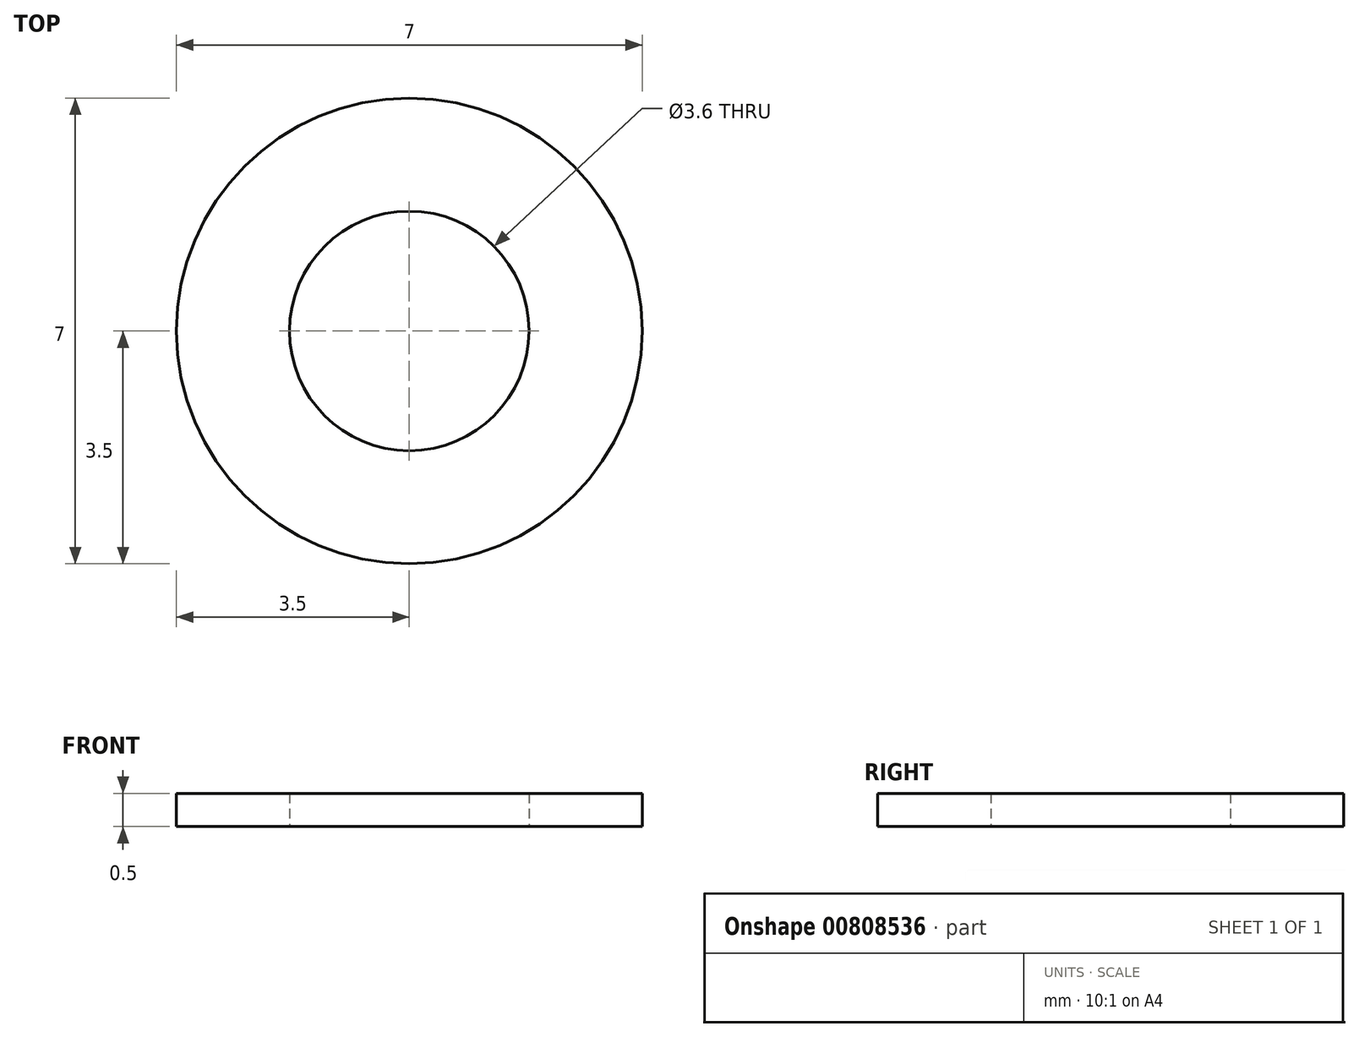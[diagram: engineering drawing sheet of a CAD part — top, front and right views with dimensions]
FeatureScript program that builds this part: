
annotation { "Feature Type Name" : "Feature", "Feature Type Description" : "" }
export const myFeature = defineFeature(function(context is Context, id is Id, definition is map)
    precondition{}
    {
        {
            var Q0;
            Q0=qCreatedBy(makeId("Top.planeOp"),FACE);
            var sketch = newSketch(context, id + "F0", { "sketchPlane" : qUnion([Q0])});
            skCircle(sketch, "E0", {"center": v(0, 0) * mm, "radius": 3.5 * mm});
            skCircle(sketch, "E1", {"center": v(0, 0) * mm, "radius": 1.8 * mm});
            skSolve(sketch);
        }
        {
            var Q0;
            Q0=makeQuery(id+"F0.imprint","IMPRINT",FACE,{"disambiguationData":[TD([[makeQuery(id+"F0.imprint","IMPRINT",EDGE,{"derivedFrom":sQuery(id+"F0.wireOp",EDGE,"E0")}),1.0]])]});
            extrude(context, id + "F1", {"entities" : qUnion([Q0]), "depth" : .5 * mm, "offsetDistance" : 25 * mm});
        }
    });
